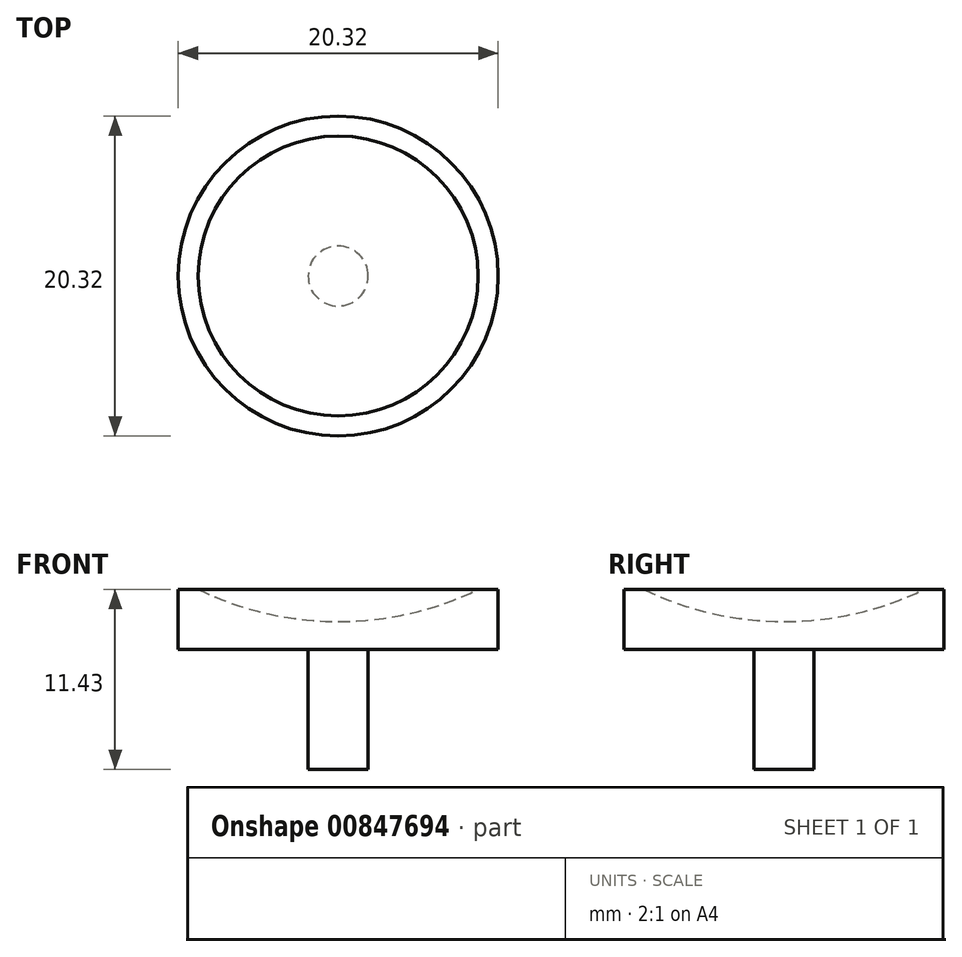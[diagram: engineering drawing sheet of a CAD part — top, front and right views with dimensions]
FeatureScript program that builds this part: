
annotation { "Feature Type Name" : "Feature", "Feature Type Description" : "" }
export const myFeature = defineFeature(function(context is Context, id is Id, definition is map)
    precondition{}
    {
        {
            var Q0;
            Q0=qCreatedBy(makeId("Top.planeOp"),FACE);
            var sketch = newSketch(context, id + "F0", { "sketchPlane" : qUnion([Q0])});
            skCircle(sketch, "E0", {"center": v(0, 0) * mm, "radius": 10.16 * mm});
            skSolve(sketch);
        }
        {
            var Q0;
            Q0=makeQuery(id+"F0.imprint","IMPRINT",FACE,{"disambiguationData":[TD([[makeQuery(id+"F0.imprint","IMPRINT",EDGE,{"derivedFrom":sQuery(id+"F0.wireOp",EDGE,"E0")}),1.0]])]});
            extrude(context, id + "F1", {"entities" : qUnion([Q0]), "depth" : 3.8 * mm, "offsetDistance" : 25.4 * mm});
        }
        {
            var Q0;
            Q0=qCreatedBy(makeId("Front.planeOp"),FACE);
            var sketch = newSketch(context, id + "F2", { "sketchPlane" : qUnion([Q0])});
            skLineSegment(sketch, "E1", {"start": v(-8.9, 3.81) * mm, "end": v(0, 3.81) * mm});
            skLineSegment(sketch, "E2", {"start": v(0, 3.81) * mm, "end": v(0, 1.78) * mm});
            skArc(sketch, "E3", {"start": v(-8.9, 3.8) * mm, "mid": v(-4.56, 2.3) * mm, "end": v(0, 1.78) * mm});
            skLineSegment(sketch, "E4", {"start": v(0, 1.78) * mm, "end": v(21.03, 1.78) * mm, "construction": true});
            skSolve(sketch);
        }
        {
            var Q0;
            Q0 = qSketchRegion(id + "F2", true);
            var Q1;
            Q1=sQuery(id+"F2.wireOp",EDGE,"E2");
            revolve(context, id + "F3", {"operationType" : NewBodyOperationType.REMOVE, "surfaceOperationType" : NewSurfaceOperationType.NEW, "entities" : qUnion([Q0]), "axis" : qUnion([Q1]), "revolveType" : RevolveType.FULL, "oppositeDirection" : true});
        }
        {
            var Q0;
            Q0=makeQuery(id+"F1.opExtrude","CAP_FACE",FACE,{"disambiguationData":[OSD([sQuery(id+"F0.wireOp",EDGE,"E0")])],"isStart":true});
            var sketch = newSketch(context, id + "F4", { "sketchPlane" : qUnion([Q0])});
            skCircle(sketch, "E5", {"center": v(0, 0) * mm, "radius": 1.9 * mm});
            skSolve(sketch);
        }
        {
            var Q0;
            Q0 = qSketchRegion(id + "F4", true);
            extrude(context, id + "F5", {"entities" : qUnion([Q0]), "operationType" : NewBodyOperationType.ADD, "depth" : 7.62 * mm, "offsetDistance" : 25.4 * mm});
        }
    });
